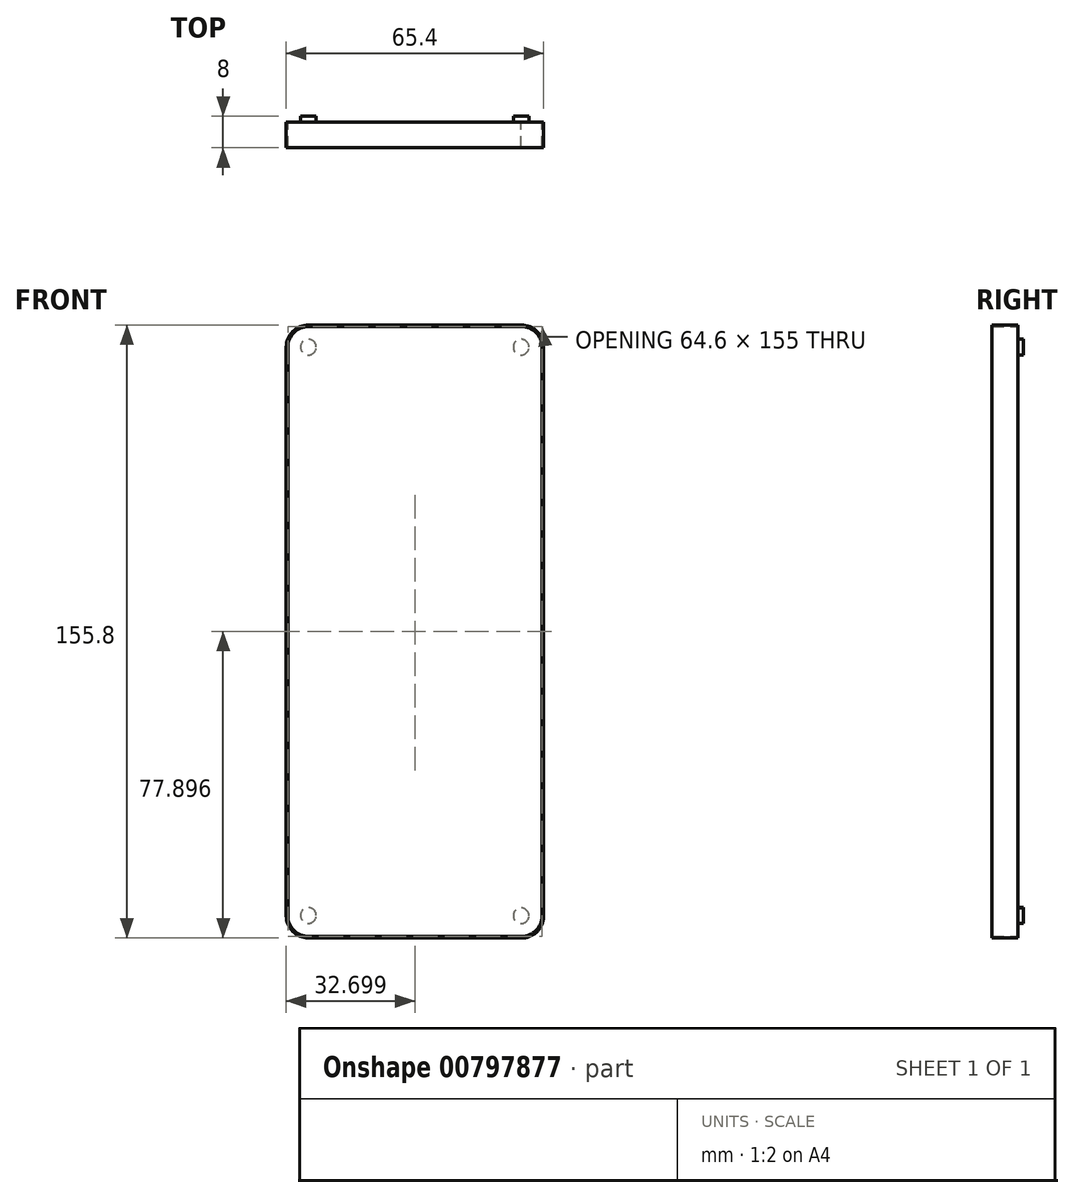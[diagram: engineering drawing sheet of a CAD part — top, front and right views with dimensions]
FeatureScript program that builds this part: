
annotation { "Feature Type Name" : "Feature", "Feature Type Description" : "" }
export const myFeature = defineFeature(function(context is Context, id is Id, definition is map)
    precondition{}
    {
        {
            var Q0;
            Q0=qCreatedBy(makeId("Front.planeOp"),FACE);
            var sketch = newSketch(context, id + "F0", { "sketchPlane" : qUnion([Q0])});
            skLineSegment(sketch, "E0", {"start": v(9.79, -32.65) * mm, "end": v(9.79, 111.79) * mm});
            skArc(sketch, "E1", {"start": v(9.79, -32.65) * mm, "mid": v(11.45, -36.66) * mm, "end": v(15.45, -38.31) * mm});
            skArc(sketch, "E2.MirrorCS", {"start": v(75.19, -32.65) * mm, "mid": v(73.5, -36.68) * mm, "end": v(69.45, -38.31) * mm});
            skLineSegment(sketch, "E3.MirrorCS", {"start": v(75.19, -32.65) * mm, "end": v(75.19, 111.79) * mm});
            skLineSegment(sketch, "E4", {"start": v(15.45, -38.31) * mm, "end": v(69.45, -38.31) * mm});
            skLineSegment(sketch, "E5", {"start": v(10.19, 111.79) * mm, "end": v(10.19, -32.65) * mm});
            skArc(sketch, "E6", {"start": v(10.19, -32.65) * mm, "mid": v(11.73, -36.37) * mm, "end": v(15.45, -37.91) * mm});
            skLineSegment(sketch, "E7", {"start": v(15.45, -37.91) * mm, "end": v(69.45, -37.91) * mm});
            skArc(sketch, "E8", {"start": v(69.45, -37.91) * mm, "mid": v(73.22, -36.4) * mm, "end": v(74.79, -32.65) * mm});
            skLineSegment(sketch, "E9", {"start": v(74.79, -32.65) * mm, "end": v(74.79, 111.79) * mm});
            skLineSegment(sketch, "E10", {"start": v(69.49, 117.49) * mm, "end": v(15.49, 117.49) * mm});
            skArc(sketch, "E11", {"start": v(15.49, 117.49) * mm, "mid": v(11.46, 115.82) * mm, "end": v(9.79, 111.79) * mm});
            skArc(sketch, "E12", {"start": v(75.19, 111.79) * mm, "mid": v(73.52, 115.82) * mm, "end": v(69.49, 117.49) * mm});
            skArc(sketch, "E13", {"start": v(10.19, 111.79) * mm, "mid": v(11.74, 115.53) * mm, "end": v(15.49, 117.09) * mm});
            skArc(sketch, "E14", {"start": v(74.79, 111.79) * mm, "mid": v(73.24, 115.53) * mm, "end": v(69.49, 117.09) * mm});
            skLineSegment(sketch, "E15", {"start": v(15.49, 117.09) * mm, "end": v(69.49, 117.09) * mm});
            skSolve(sketch);
        }
        {
            var Q0;
            Q0=qCreatedBy(makeId("Front.planeOp"),FACE);
            var sketch = newSketch(context, id + "F1", { "sketchPlane" : qUnion([Q0])});
            skCircle(sketch, "E16", {"center": v(69.47, 111.83) * mm, "radius": 2 * mm});
            skCircle(sketch, "E17", {"center": v(15.4, 111.83) * mm, "radius": 2 * mm});
            skCircle(sketch, "E18", {"center": v(69.47, -32.63) * mm, "radius": 2 * mm});
            skCircle(sketch, "E19", {"center": v(15.4, -32.56) * mm, "radius": 2 * mm});
            skSolve(sketch);
        }
        {
            var Q0;
            {var subQ0=sQuery(id+"F0.wireOp",EDGE,"E12");Q0=makeQuery(id+"F0.imprint","IMPRINT",FACE,{"disambiguationData":[TD([[makeQuery(id+"F0.imprint","IMPRINT",EDGE,{"derivedFrom":subQ0}),-1.0]])]});}
            var Q1;
            Q1=makeQuery(id+"F0.imprint","IMPRINT",FACE,{"disambiguationData":[TD([[makeQuery(id+"F0.imprint","IMPRINT",EDGE,{"derivedFrom":sQuery(id+"F0.wireOp",EDGE,"E0")}),-1.0]])]});
            extrude(context, id + "F2", {"entities" : qUnion([Q0, Q1]), "depth" : 6.5 * mm, "offsetDistance" : 25 * mm});
        }
        {
            var Q0;
            Q0=makeQuery(id+"F0.imprint","IMPRINT",FACE,{"disambiguationData":[TD([[makeQuery(id+"F0.imprint","IMPRINT",EDGE,{"derivedFrom":sQuery(id+"F0.wireOp",EDGE,"E5")}),1.0]])]});
            extrude(context, id + "F3", {"entities" : qUnion([Q0]), "depth" : 0.1 * mm, "offsetDistance" : 25 * mm});
        }
        {
            var Q0;
            Q0=makeQuery(id+"F1.imprint","IMPRINT",FACE,{"disambiguationData":[TD([[makeQuery(id+"F1.imprint","IMPRINT",EDGE,{"derivedFrom":sQuery(id+"F1.wireOp",EDGE,"E19")}),1.0]])]});
            var Q1;
            Q1=makeQuery(id+"F1.imprint","IMPRINT",FACE,{"disambiguationData":[TD([[makeQuery(id+"F1.imprint","IMPRINT",EDGE,{"derivedFrom":sQuery(id+"F1.wireOp",EDGE,"E18")}),1.0]])]});
            var Q2;
            Q2=makeQuery(id+"F1.imprint","IMPRINT",FACE,{"disambiguationData":[TD([[makeQuery(id+"F1.imprint","IMPRINT",EDGE,{"derivedFrom":sQuery(id+"F1.wireOp",EDGE,"E16")}),1.0]])]});
            var Q3;
            Q3=makeQuery(id+"F1.imprint","IMPRINT",FACE,{"disambiguationData":[TD([[makeQuery(id+"F1.imprint","IMPRINT",EDGE,{"derivedFrom":sQuery(id+"F1.wireOp",EDGE,"E17")}),1.0]])]});
            extrude(context, id + "F4", {"entities" : qUnion([Q0, Q1, Q2, Q3]), "operationType" : NewBodyOperationType.ADD, "oppositeDirection" : true, "depth" : 1.5 * mm, "offsetDistance" : 25 * mm});
        }
    });
